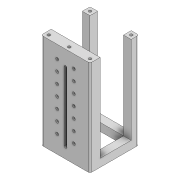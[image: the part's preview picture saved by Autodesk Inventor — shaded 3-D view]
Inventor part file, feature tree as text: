
AUTODESK INVENTOR PART (.ipt)
format: ipt  version: 2022 (Build 260153000, 153)  size: 193,536 bytes
history: native  units: mm
features: extrude x6, sketch x6, fillet x1
ambient origin geometry x8: Origin, YZ Plane, XZ Plane, XY Plane, X Axis, Y Axis, Z Axis, Center Point
bodies: Solid1 (feature_tree)
feature tree (13):
  extrude  "Extrusion1"  Depth=49.8mm
  extrude  "Extrusion2"  Depth=8.0mm TaperAngle=0.0deg
  extrude  "Extrusion3"  Depth=97.0mm TaperAngle=0.0deg
  extrude  "Extrusion4"  Depth=2.9mm
  extrude  "Extrusion5"  Depth=23.45mm
  fillet  "Fillet1"  [1 undecoded]
  extrude  "Extrusion6"  Depth=10.0mm
  sketch  "Sketch1"  dims[d0=49.8mm d1=49.8mm]
  sketch  "Sketch3"  dims[d2=7.8mm d3=8.0mm d4=0.0mm]
  sketch  "Sketch4"  dims[d6=10.23mm d7=97.0mm d8=0.0mm]
  sketch  "Sketch5"  dims[d9=2.9mm d10=70.0mm]
  sketch  "Sketch6"  dims[d11=23.45mm d12=11.0mm d13=0.0mm d14=0.0mm]
  sketch  "Sketch7"  dims[d15=2.9mm d16=7.05mm d17=2.9mm d18=7.05mm d19=13.0mm d20=13.0mm d21=70.0mm d23=11.0mm d24=10.0mm d26=10.0mm d28=2.8mm d29=2.8mm d30=20.0mm d31=0.0mm d35=10.0mm d36=0.0mm d37=2.8mm d38=3.7mm d39=24.9mm d40=2.0mm d41=10.0mm d42=0.0mm]
note: 1 required parameter value undecoded (feature->parameter linkage not recoverable at this tier; creation-order binding heuristic only, values carry confidence <= 0.55)
